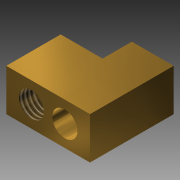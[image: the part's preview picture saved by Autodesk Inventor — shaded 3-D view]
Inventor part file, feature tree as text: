
AUTODESK INVENTOR PART (.ipt)
format: ipt  version: 2013 (Build 170138000, 138)  size: 122,880 bytes
history: native  units: mm
features: sketch x3, extrude x2, hole x1, thread x1
ambient origin geometry x8: Origin, YZ Plane, XZ Plane, XY Plane, X Axis, Y Axis, Z Axis, Center Point
bodies: Solid1 (feature_tree)
feature tree (7):
  extrude  "Extrusion1"  Depth=20.0mm
  extrude  "Extrusion2"  Depth=7.0mm
  hole  "Hole1"  [1 undecoded]
  thread  "Thread1"  [1 undecoded]
  sketch  "Sketch1"  dims[d0=20.0mm d2=20.0mm]
  sketch  "Sketch2"  dims[d3=10.0mm d4=7.0mm]
  sketch  "Sketch3"  dims[d5=10.0mm d6=0.0mm d7=6.0mm d9=6.0mm d10=5.0mm d11=6.0mm d12=6.0mm d13=22.0mm d14=0.0mm d15=2.5mm d17=2.5mm d18=10.0mm d19=2.5mm d20=6.0mm d21=4.0mm d22=2.0mm d23=90.0deg d24=3.0mm d25=20.594885mm d26=10.0mm d27=0.0mm]
note: 2 required parameter values undecoded (feature->parameter linkage not recoverable at this tier; creation-order binding heuristic only, values carry confidence <= 0.55)
